# Revit family: FireFighting_Mounting-Post_Galvin_383263
name_source: partatom
category: Mechanical Equipment
revit_build: Autodesk Revit MEP 2012 (Build: 20110916_2132(x64)
units: mm (PartAtom-declared; Revit-internal decimal feet)

## types (1)
- 383263
    Assembly Code = D4030
    Description = Galvanised Bolt Down Mounting Post for Fire Hose Reels
    DimDepth = 300 mm
    DimHeight = 1600 mm  [stored 5.24934 ft]
    DimWidth = 300 mm
    FilterObject_ANZRS = 383263
    Instructions = http://www.galvinengineering.com.au
    Keynote = 10520
    Manufacturer = Galvin Engineering
    Material = Metal_Fire-Fighting_Galvanised-Iron_15400
    Model = 383263
    ModifiedIssue_ANZRS = 20140514 $
    StyleOrType_ANZRS = Fire Fighting Equipment
    Type Comments = 383263
    URL = www.galvinengineering.com.au

note: [stored X ft] marks values corroborated as IEEE doubles in the binary element streams (Revit-internal decimal feet)

## geometry (parser evidence)
native form markers: Blend x2, Sweep x1
no freeform markers — native parametric forms only
